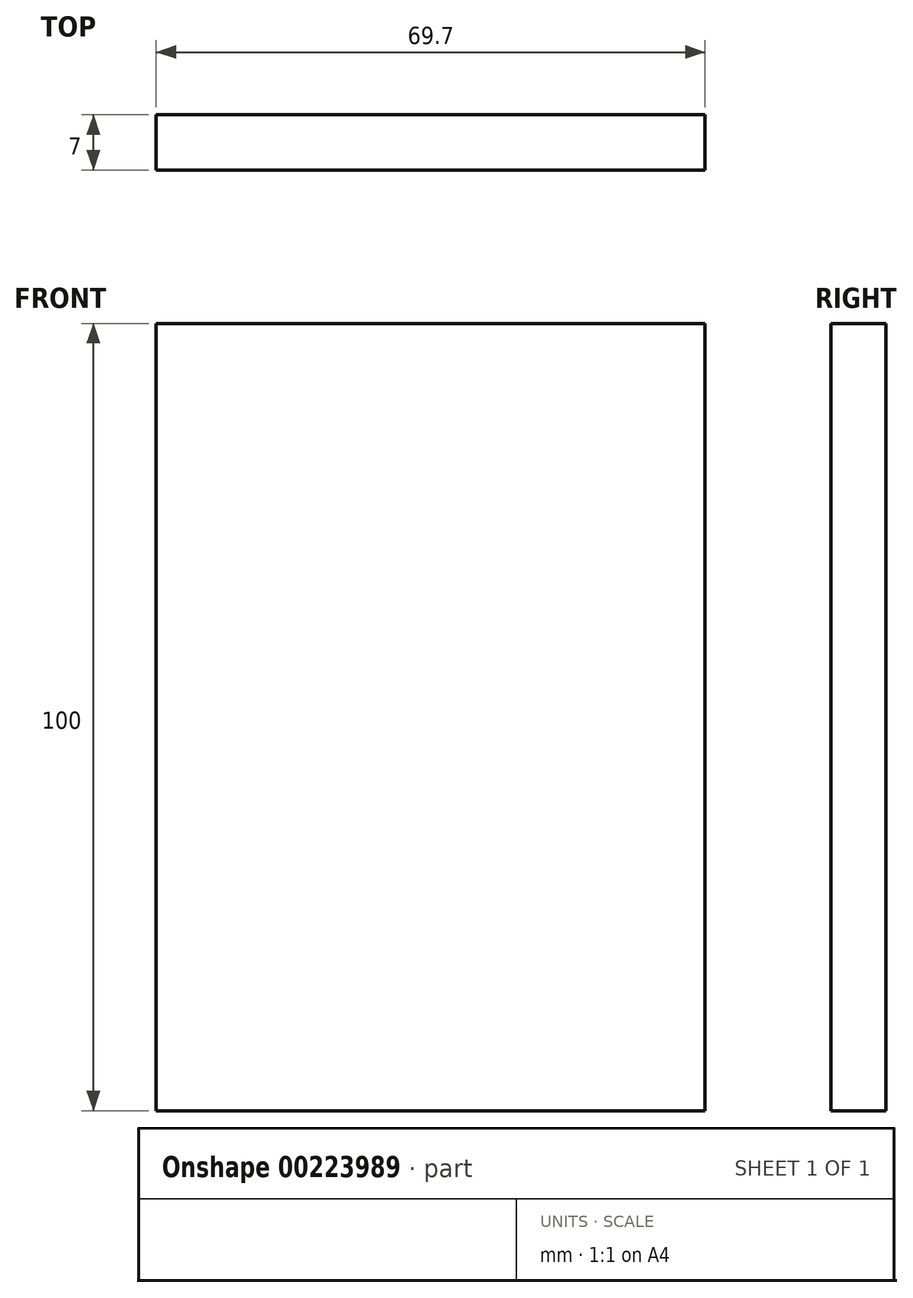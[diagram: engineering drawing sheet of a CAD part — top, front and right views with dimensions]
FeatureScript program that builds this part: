
annotation { "Feature Type Name" : "Feature", "Feature Type Description" : "" }
export const myFeature = defineFeature(function(context is Context, id is Id, definition is map)
    precondition{}
    {
        {
            var Q0;
            Q0=qCreatedBy(makeId("Front.planeOp"),FACE);
            var sketch = newSketch(context, id + "F0", { "sketchPlane" : qUnion([Q0])});
            skLineSegment(sketch, "E0.bottom", {"start": v(34.85, -50) * mm, "end": v(-34.85, -50) * mm});
            skLineSegment(sketch, "E0.top", {"start": v(34.85, 50) * mm, "end": v(-34.85, 50) * mm});
            skLineSegment(sketch, "E0.left", {"start": v(34.85, -50) * mm, "end": v(34.85, 50) * mm});
            skLineSegment(sketch, "E0.right", {"start": v(-34.85, -50) * mm, "end": v(-34.85, 50) * mm});
            skPoint(sketch, "E0.middle", {"position": v(0, 0) * mm});
            skSolve(sketch);
        }
        {
            var Q0;
            Q0 = qSketchRegion(id + "F0", true);
            extrude(context, id + "F1", {"entities" : qUnion([Q0]), "depth" : 7 * mm});
        }
    });
